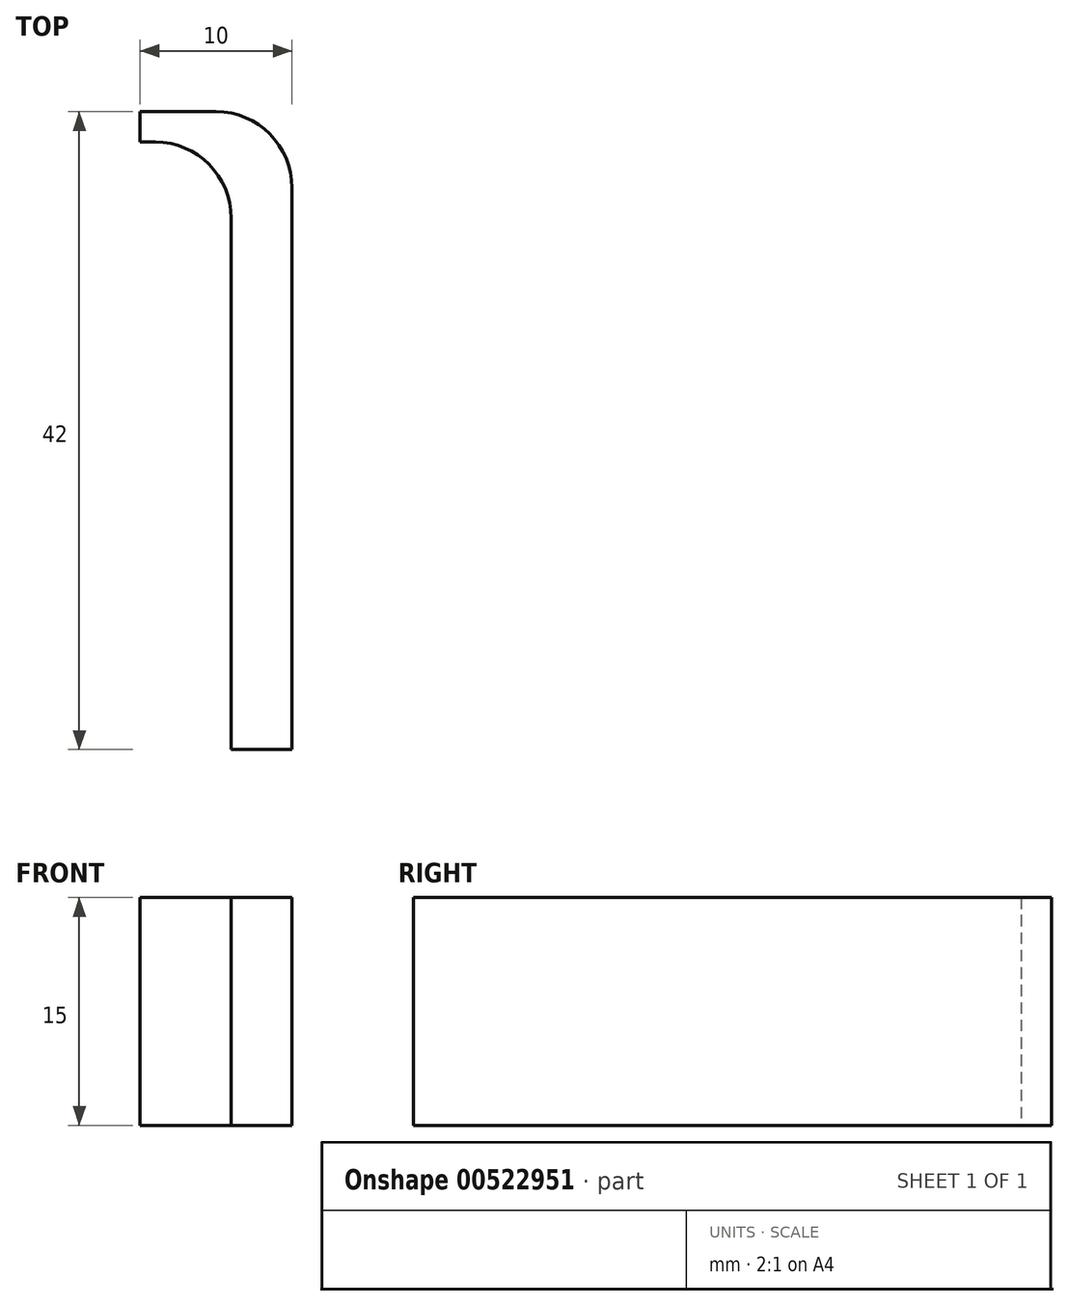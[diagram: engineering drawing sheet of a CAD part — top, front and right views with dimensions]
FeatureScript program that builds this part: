
annotation { "Feature Type Name" : "Feature", "Feature Type Description" : "" }
export const myFeature = defineFeature(function(context is Context, id is Id, definition is map)
    precondition{}
    {
        {
            var Q0;
            Q0=qCreatedBy(makeId("Top.planeOp"),FACE);
            var sketch = newSketch(context, id + "F0", { "sketchPlane" : qUnion([Q0])});
            skLineSegment(sketch, "E0.bottom", {"start": v(2, -20) * mm, "end": v(-2, -20) * mm});
            skLineSegment(sketch, "E0.top", {"start": v(2, 20) * mm, "end": v(-2, 20) * mm, "construction": true});
            skLineSegment(sketch, "E0.left", {"start": v(2, -20) * mm, "end": v(2, 20) * mm});
            skLineSegment(sketch, "E0.right", {"start": v(-2, -20) * mm, "end": v(-2, 15) * mm});
            skPoint(sketch, "E0.middle", {"position": v(0, 0) * mm});
            skLineSegment(sketch, "E1.bottom", {"start": v(-7, 20) * mm, "end": v(-8, 20) * mm});
            skLineSegment(sketch, "E1.top", {"start": v(-3, 22) * mm, "end": v(-8, 22) * mm});
            skLineSegment(sketch, "E1.left", {"start": v(2, 17) * mm, "end": v(2, 20) * mm, "construction": true});
            skLineSegment(sketch, "E1.right", {"start": v(-8, 20) * mm, "end": v(-8, 22) * mm});
            skPoint(sketch, "E2.visualSharp", {"position": v(-2, 20) * mm});
            skArc(sketch, "E2.filletArc", {"start": v(-2, 15) * mm, "mid": v(-3.46, 18.54) * mm, "end": v(-7, 20) * mm});
            skPoint(sketch, "E3.visualSharp", {"position": v(2, 22) * mm});
            skArc(sketch, "E3.filletArc", {"start": v(2, 17) * mm, "mid": v(0.54, 20.54) * mm, "end": v(-3, 22) * mm});
            skSolve(sketch);
        }
        {
            var Q0;
            Q0 = qSketchRegion(id + "F0", true);
            extrude(context, id + "F1", {"entities" : qUnion([Q0]), "endBound" : BoundingType.SYMMETRIC, "depth" : 15 * mm, "offsetDistance" : 25 * mm});
        }
    });
